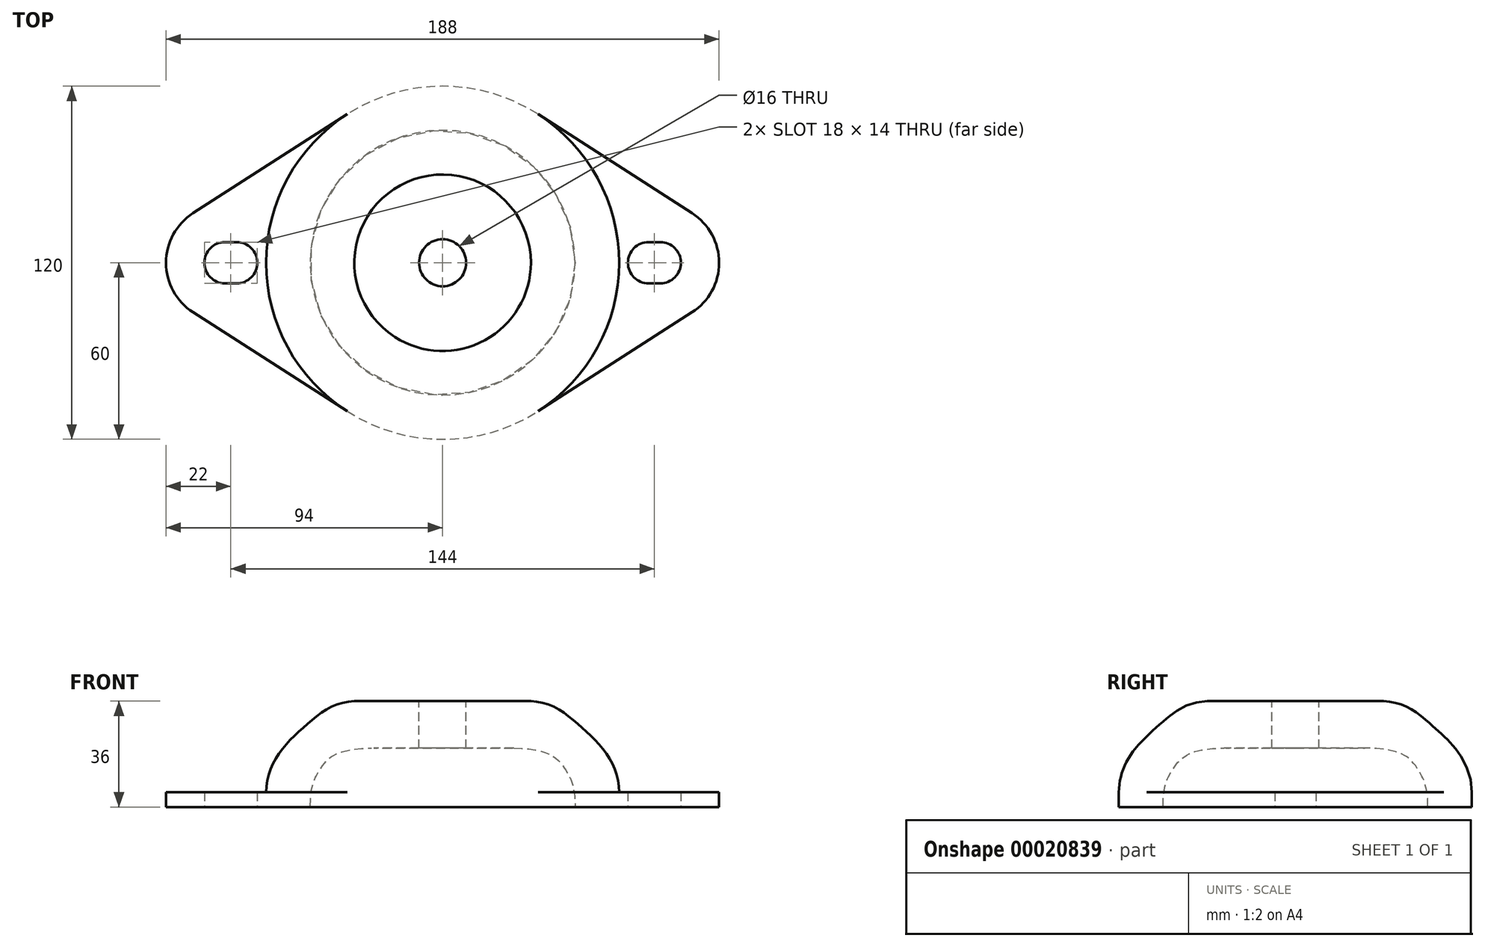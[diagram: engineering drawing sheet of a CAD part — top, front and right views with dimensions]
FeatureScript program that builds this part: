
annotation { "Feature Type Name" : "Feature", "Feature Type Description" : "" }
export const myFeature = defineFeature(function(context is Context, id is Id, definition is map)
    precondition{}
    {
        {
            var Q0;
            Q0=qCreatedBy(makeId("Top.planeOp"),FACE);
            var sketch = newSketch(context, id + "F0", { "sketchPlane" : qUnion([Q0])});
            skArc(sketch, "E0", {"start": v(-32.43, 50.48) * mm, "mid": v(-52.66, 28.76) * mm, "end": v(-60, 0) * mm});
            skLineSegment(sketch, "E1", {"start": v(-32.43, 50.48) * mm, "end": v(-84.81, 16.83) * mm});
            skArc(sketch, "E2", {"start": v(-84.81, 16.83) * mm, "mid": v(-91.55, 9.59) * mm, "end": v(-94, 0) * mm});
            skArc(sketch, "E3.MirrorCS", {"start": v(-32.43, -50.48) * mm, "mid": v(-52.66, -28.76) * mm, "end": v(-60, 0) * mm});
            skLineSegment(sketch, "E4.MirrorCS", {"start": v(-32.43, -50.48) * mm, "end": v(-84.81, -16.83) * mm});
            skArc(sketch, "E5.MirrorCS", {"start": v(-84.81, -16.83) * mm, "mid": v(-91.55, -9.59) * mm, "end": v(-94, 0) * mm});
            skLineSegment(sketch, "E6", {"start": v(-70, 0) * mm, "end": v(-74, 0) * mm, "construction": true});
            skArc(sketch, "E7.0.startCap", {"start": v(-70, 7) * mm, "mid": v(-63, 0) * mm, "end": v(-70, -7) * mm});
            skArc(sketch, "E7.0.endCap", {"start": v(-74, -7) * mm, "mid": v(-81, 0) * mm, "end": v(-74, 7) * mm});
            skLineSegment(sketch, "E7.0.left", {"start": v(-70, -7) * mm, "end": v(-74, -7) * mm});
            skLineSegment(sketch, "E7.0.right", {"start": v(-70, 7) * mm, "end": v(-74, 7) * mm});
            skSolve(sketch);
        }
        {
            var Q0;
            Q0=qCreatedBy(makeId("Front.planeOp"),FACE);
            var sketch = newSketch(context, id + "F1", { "sketchPlane" : qUnion([Q0])});
            skFitSpline(sketch, "E8", {"points": [v(-24.2, 20) * mm, v(-41.52, 13.03) * mm, v(-45, 0) * mm], "startDerivative": vector(-67.06, 0) * mm, "endDerivative": vector(0.4, -45.95) * mm});
            skLineSegment(sketch, "E9", {"start": v(-60, 0) * mm, "end": v(-45, 0) * mm});
            skLineSegment(sketch, "E10", {"start": v(-30, 36) * mm, "end": v(-8, 36) * mm});
            skLineSegment(sketch, "E11", {"start": v(-8, 36) * mm, "end": v(-8, 20) * mm});
            skLineSegment(sketch, "E12", {"start": v(-8, 20) * mm, "end": v(-24.2, 20) * mm});
            skLineSegment(sketch, "E13", {"start": v(0, 66.61) * mm, "end": v(0, -29.52) * mm, "construction": true});
            skLineSegment(sketch, "E14", {"start": v(-60, 0) * mm, "end": v(-60, 5) * mm});
            skFitSpline(sketch, "E15", {"points": [v(-60, 5) * mm, v(-46.32, 27.87) * mm, v(-30, 36) * mm], "startDerivative": vector(0.52, 59.5) * mm, "endDerivative": vector(48.63, 2.47) * mm});
            skSolve(sketch);
        }
        {
            var Q0;
            Q0=makeQuery(id+"F0.imprint","IMPRINT",FACE,{"disambiguationData":[TD([[makeQuery(id+"F0.imprint","IMPRINT",EDGE,{"derivedFrom":sQuery(id+"F0.wireOp",EDGE,"E0")}),-1.0]])]});
            extrude(context, id + "F2", {"entities" : qUnion([Q0]), "depth" : 5 * mm});
        }
        {
            var Q0;
            Q0=makeQuery(id+"F2.opExtrude","SWEPT_BODY",BODY,{"disambiguationData":[OSD([sQuery(id+"F0.wireOp",EDGE,"E0"),sQuery(id+"F0.wireOp",EDGE,"E1"),sQuery(id+"F0.wireOp",EDGE,"E2"),sQuery(id+"F0.wireOp",EDGE,"E3.MirrorCS"),sQuery(id+"F0.wireOp",EDGE,"E4.MirrorCS"),sQuery(id+"F0.wireOp",EDGE,"E5.MirrorCS")])]});
            var Q1;
            Q1=qCreatedBy(makeId("Right.planeOp"),FACE);
            mirror(context, id + "F3", {"entities" : qUnion([Q0]), "mirrorPlane" : qUnion([Q1])});
        }
        {
            var Q0;
            Q0 = qSketchRegion(id + "F1", true);
            var Q1;
            Q1=sQuery(id+"F1.wireOp",EDGE,"E13");
            revolve(context, id + "F4", {"operationType" : NewBodyOperationType.ADD, "entities" : qUnion([Q0]), "axis" : qUnion([Q1]), "revolveType" : RevolveType.FULL});
        }
    });
